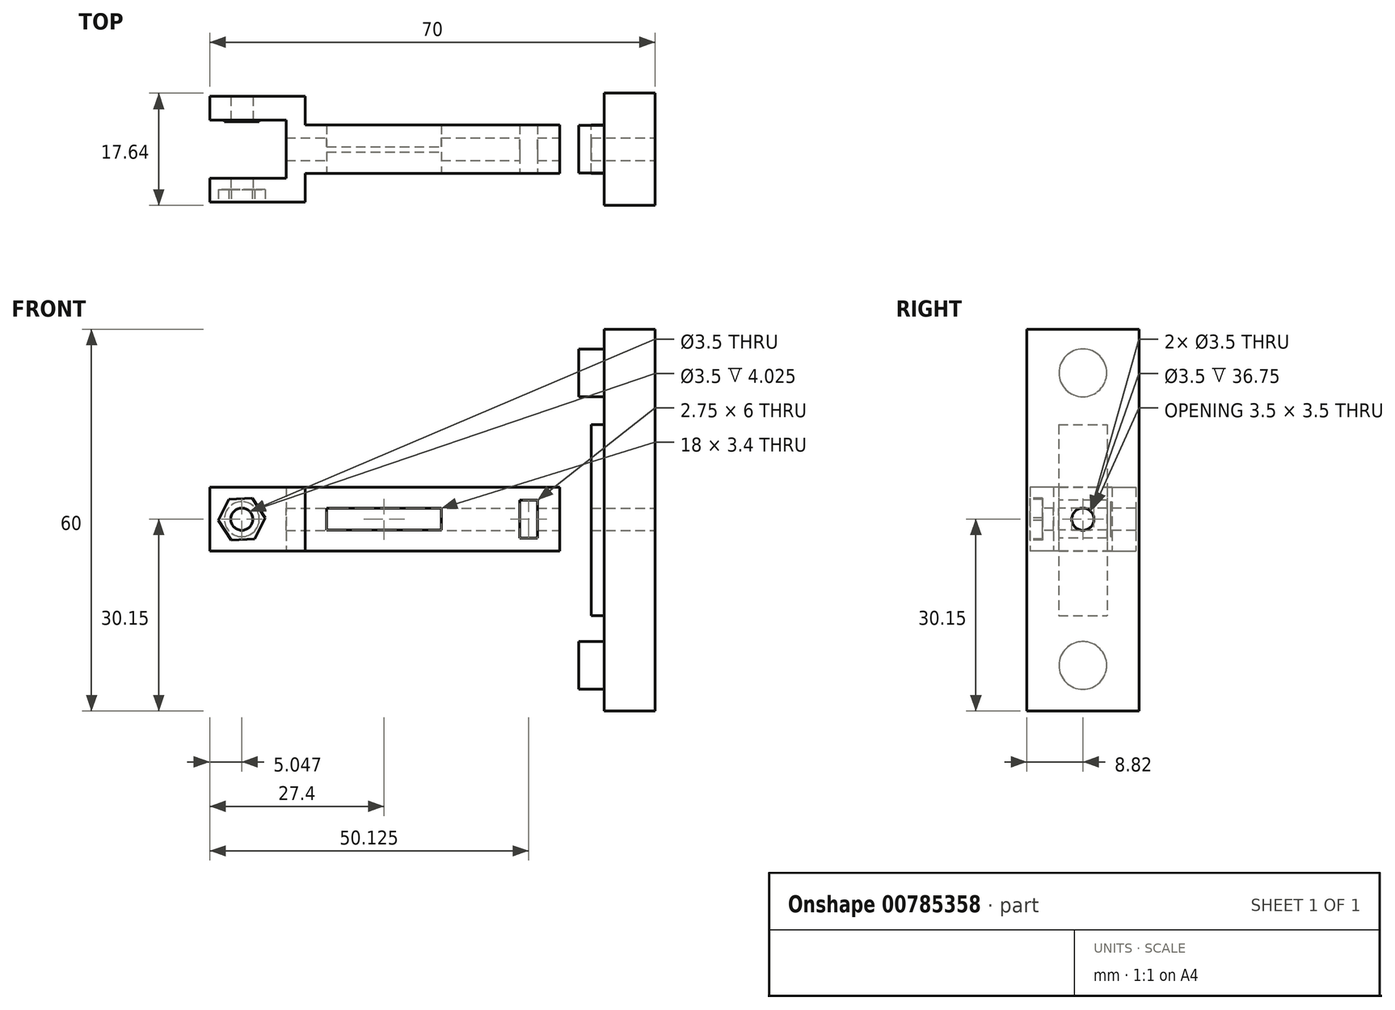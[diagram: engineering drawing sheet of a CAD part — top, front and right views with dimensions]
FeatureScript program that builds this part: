
annotation { "Feature Type Name" : "Feature", "Feature Type Description" : "" }
export const myFeature = defineFeature(function(context is Context, id is Id, definition is map)
    precondition{}
    {
        {
            var Q0;
            Q0=qCreatedBy(makeId("Top.planeOp"),FACE);
            var sketch = newSketch(context, id + "F0", { "sketchPlane" : qUnion([Q0])});
            skLineSegment(sketch, "E0.bottom", {"start": v(0, 0) * mm, "end": v(40, 0) * mm});
            skLineSegment(sketch, "E0.top", {"start": v(0, -3.83) * mm, "end": v(40, -3.83) * mm});
            skLineSegment(sketch, "E0.left", {"start": v(0, 0) * mm, "end": v(0, -3.83) * mm});
            skLineSegment(sketch, "E0.right", {"start": v(40, 0) * mm, "end": v(40, -3.83) * mm});
            skLineSegment(sketch, "E1.bottom", {"start": v(-3, 0) * mm, "end": v(0, 0) * mm});
            skLineSegment(sketch, "E1.top", {"start": v(-15, -8.32) * mm, "end": v(0, -8.32) * mm});
            skLineSegment(sketch, "E1.left", {"start": v(-15, -4.6) * mm, "end": v(-15, -8.32) * mm});
            skLineSegment(sketch, "E1.right", {"start": v(0, 0) * mm, "end": v(0, -8.32) * mm});
            skLineSegment(sketch, "E2.top", {"start": v(-15, -4.6) * mm, "end": v(-3, -4.6) * mm});
            skLineSegment(sketch, "E2.right", {"start": v(-3, 0) * mm, "end": v(-3, -4.6) * mm});
            skLineSegment(sketch, "E3.MirrorCS", {"start": v(0, 0) * mm, "end": v(0, 3.83) * mm});
            skLineSegment(sketch, "E4.MirrorCS", {"start": v(0, 0) * mm, "end": v(0, 8.32) * mm});
            skLineSegment(sketch, "E5.MirrorCS", {"start": v(-15, 4.6) * mm, "end": v(-15, 8.32) * mm});
            skLineSegment(sketch, "E6.MirrorCS", {"start": v(-3, 0) * mm, "end": v(-3, 4.6) * mm});
            skLineSegment(sketch, "E7.MirrorCS", {"start": v(-15, 8.32) * mm, "end": v(0, 8.32) * mm});
            skLineSegment(sketch, "E8.MirrorCS", {"start": v(-15, 4.6) * mm, "end": v(-3, 4.6) * mm});
            skLineSegment(sketch, "E9.MirrorCS", {"start": v(40, 0) * mm, "end": v(40, 3.83) * mm});
            skLineSegment(sketch, "E10.MirrorCS", {"start": v(0, 3.83) * mm, "end": v(40, 3.83) * mm});
            skSolve(sketch);
        }
        {
            var Q0;
            Q0=makeQuery(id+"F0.imprint","IMPRINT",FACE,{"disambiguationData":[TD([[makeQuery(id+"F0.imprint","IMPRINT",EDGE,{"derivedFrom":sQuery(id+"F0.wireOp",EDGE,"E0.left")}),-1.0]])]});
            var Q1;
            Q1=makeQuery(id+"F0.imprint","IMPRINT",FACE,{"disambiguationData":[TD([[makeQuery(id+"F0.imprint","IMPRINT",EDGE,{"derivedFrom":sQuery(id+"F0.wireOp",EDGE,"E1.bottom")}),1.0]])]});
            var Q2;
            Q2=makeQuery(id+"F0.imprint","IMPRINT",FACE,{"disambiguationData":[TD([[makeQuery(id+"F0.imprint","IMPRINT",EDGE,{"derivedFrom":sQuery(id+"F0.wireOp",EDGE,"E0.bottom")}),1.0]])]});
            var Q3;
            Q3=makeQuery(id+"F0.imprint","IMPRINT",FACE,{"disambiguationData":[TD([[makeQuery(id+"F0.imprint","IMPRINT",EDGE,{"derivedFrom":sQuery(id+"F0.wireOp",EDGE,"E0.bottom")}),-1.0]])]});
            extrude(context, id + "F1", {"entities" : qUnion([Q0, Q1, Q2, Q3]), "depth" : 10 * mm});
        }
        {
            var Q0;
            Q0=makeQuery(id+"F1.opExtrude","SWEPT_FACE",FACE,{"disambiguationData":[OSD([sQuery(id+"F0.wireOp",EDGE,"E1.top")])]});
            var sketch = newSketch(context, id + "F2", { "sketchPlane" : qUnion([Q0])});
            skCircle(sketch, "E11", {"center": v(-9.95, 5) * mm, "radius": 1.75 * mm});
            skSolve(sketch);
        }
        {
            var Q0;
            Q0=makeQuery(id+"F2.imprint","IMPRINT",FACE,{"disambiguationData":[TD([[makeQuery(id+"F2.imprint","IMPRINT",EDGE,{"derivedFrom":sQuery(id+"F2.wireOp",EDGE,"E11")}),1.0]])]});
            extrude(context, id + "F3", {"entities" : qUnion([Q0]), "operationType" : NewBodyOperationType.REMOVE, "endBound" : BoundingType.THROUGH_ALL, "oppositeDirection" : true, "depth" : 25 * mm});
        }
        {
            var Q0;
            Q0=makeQuery(id+"F1.opExtrude","SWEPT_FACE",FACE,{"disambiguationData":[OSD([sQuery(id+"F0.wireOp",EDGE,"E0.top")])]});
            var sketch = newSketch(context, id + "F4", { "sketchPlane" : qUnion([Q0])});
            skLineSegment(sketch, "E12.bottom", {"start": v(3.4, 3.3) * mm, "end": v(21.4, 3.3) * mm});
            skLineSegment(sketch, "E12.top", {"start": v(3.4, 6.7) * mm, "end": v(21.4, 6.7) * mm});
            skLineSegment(sketch, "E12.left", {"start": v(3.4, 3.3) * mm, "end": v(3.4, 6.7) * mm});
            skLineSegment(sketch, "E12.right", {"start": v(21.4, 3.3) * mm, "end": v(21.4, 6.7) * mm});
            skLineSegment(sketch, "E13.bottom", {"start": v(33.75, 8) * mm, "end": v(36.5, 8) * mm});
            skLineSegment(sketch, "E13.top", {"start": v(33.75, 2) * mm, "end": v(36.5, 2) * mm});
            skLineSegment(sketch, "E13.left", {"start": v(33.75, 8) * mm, "end": v(33.75, 2) * mm});
            skLineSegment(sketch, "E13.right", {"start": v(36.5, 8) * mm, "end": v(36.5, 2) * mm});
            skSolve(sketch);
        }
        {
            var Q0;
            Q0=makeQuery(id+"F4.imprint","IMPRINT",FACE,{"disambiguationData":[TD([[makeQuery(id+"F4.imprint","IMPRINT",EDGE,{"derivedFrom":sQuery(id+"F4.wireOp",EDGE,"E12.bottom")}),1.0]])]});
            var Q1;
            Q1=makeQuery(id+"F4.imprint","IMPRINT",FACE,{"disambiguationData":[TD([[makeQuery(id+"F4.imprint","IMPRINT",EDGE,{"derivedFrom":sQuery(id+"F4.wireOp",EDGE,"E13.bottom")}),-1.0]])]});
            extrude(context, id + "F5", {"entities" : qUnion([Q0, Q1]), "operationType" : NewBodyOperationType.REMOVE, "endBound" : BoundingType.THROUGH_ALL, "oppositeDirection" : true, "depth" : 25 * mm});
        }
        {
            var Q0;
            Q0=makeQuery(id+"F1.opExtrude","SWEPT_FACE",FACE,{"disambiguationData":[OSD([sQuery(id+"F0.wireOp",EDGE,"E0.right"),sQuery(id+"F0.wireOp",EDGE,"E9.MirrorCS")])]});
            var sketch = newSketch(context, id + "F6", { "sketchPlane" : qUnion([Q0])});
            skCircle(sketch, "E14", {"center": v(0, 5) * mm, "radius": 1.75 * mm});
            skSolve(sketch);
        }
        {
            var Q0;
            Q0=makeQuery(id+"F6.imprint","IMPRINT",FACE,{"disambiguationData":[TD([[makeQuery(id+"F6.imprint","IMPRINT",EDGE,{"derivedFrom":sQuery(id+"F6.wireOp",EDGE,"E14")}),1.0]])]});
            extrude(context, id + "F7", {"entities" : qUnion([Q0]), "operationType" : NewBodyOperationType.REMOVE, "oppositeDirection" : true, "depth" : 15 * mm});
        }
        {
            var Q0;
            Q0=makeQuery(id+"F1.opExtrude","SWEPT_FACE",FACE,{"disambiguationData":[OSD([sQuery(id+"F0.wireOp",EDGE,"E0.right"),sQuery(id+"F0.wireOp",EDGE,"E9.MirrorCS")])]});
            cPlane(context, id + "F8", {"entities" : qUnion([Q0]), "cplaneType" : CPlaneType.OFFSET, "offset" : 5 * mm, "width" : 150 * mm, "height" : 150 * mm});
        }
        {
            var Q0;
            Q0=qCreatedBy(id+"F8.planeOp",FACE);
            var sketch = newSketch(context, id + "F9", { "sketchPlane" : qUnion([Q0])});
            skLineSegment(sketch, "E15.0", {"start": v(3.83, 10) * mm, "end": v(3.83, 0) * mm});
            skLineSegment(sketch, "E16.0", {"start": v(-3.83, 10) * mm, "end": v(-3.83, 0) * mm});
            skLineSegment(sketch, "E17.bottom", {"start": v(-3.82, 19.85) * mm, "end": v(3.82, 19.85) * mm});
            skLineSegment(sketch, "E17.top", {"start": v(-3.82, -10.15) * mm, "end": v(3.82, -10.15) * mm});
            skLineSegment(sketch, "E17.left", {"start": v(-3.83, 19.85) * mm, "end": v(-3.82, -10.15) * mm});
            skLineSegment(sketch, "E17.right", {"start": v(3.82, 19.85) * mm, "end": v(3.83, -10.15) * mm});
            skPoint(sketch, "E18.oppositeSnap0", {"position": v(3.83, 4.85) * mm});
            skLineSegment(sketch, "E18.bottom", {"start": v(3.83, 4.85) * mm, "end": v(3.83, 4.85) * mm});
            skLineSegment(sketch, "E18.top", {"start": v(3.83, 4.85) * mm, "end": v(3.83, 4.85) * mm});
            skLineSegment(sketch, "E18.left", {"start": v(3.83, 4.85) * mm, "end": v(3.83, 4.85) * mm});
            skLineSegment(sketch, "E18.right", {"start": v(3.83, 4.85) * mm, "end": v(3.83, 4.85) * mm});
            skSolve(sketch);
        }
        {
            var Q0;
            {var subQ0=sQuery(id+"F9.wireOp",EDGE,"E17.bottom");Q0=makeQuery(id+"F9.imprint","IMPRINT",FACE,{"disambiguationData":[TD([[makeQuery(id+"F9.imprint","IMPRINT",EDGE,{"derivedFrom":subQ0}),-1.0]])]});}
            extrude(context, id + "F10", {"entities" : qUnion([Q0]), "depth" : 2 * mm});
        }
        {
            var Q0;
            Q0=makeQuery(id+"F10.opExtrude","CAP_FACE",FACE,{"disambiguationData":[OSD([sQuery(id+"F9.wireOp",EDGE,"E17.bottom"),sQuery(id+"F9.wireOp",EDGE,"E17.top"),sQuery(id+"F9.wireOp",EDGE,"E17.left"),sQuery(id+"F9.wireOp",EDGE,"E17.right")])],"isStart":false});
            var sketch = newSketch(context, id + "F11", { "sketchPlane" : qUnion([Q0])});
            skLineSegment(sketch, "E19.bottom", {"start": v(8.82, 34.85) * mm, "end": v(-8.83, 34.85) * mm});
            skLineSegment(sketch, "E19.top", {"start": v(8.83, -25.15) * mm, "end": v(-8.82, -25.15) * mm});
            skLineSegment(sketch, "E19.left", {"start": v(8.82, 34.85) * mm, "end": v(8.83, -25.15) * mm});
            skLineSegment(sketch, "E19.right", {"start": v(-8.83, 34.85) * mm, "end": v(-8.82, -25.15) * mm});
            skSolve(sketch);
        }
        {
            var Q0;
            Q0=qSketchRegion(id+"F11",true);
            extrude(context, id + "F12", {"entities" : qUnion([Q0]), "operationType" : NewBodyOperationType.ADD, "depth" : 8 * mm});
        }
        {
            var Q0;
            Q0=makeQuery(id+"F12.opExtrude","CAP_FACE",FACE,{"disambiguationData":[OSD([sQuery(id+"F11.wireOp",EDGE,"E19.bottom"),sQuery(id+"F11.wireOp",EDGE,"E19.top"),sQuery(id+"F11.wireOp",EDGE,"E19.left"),sQuery(id+"F11.wireOp",EDGE,"E19.right")])],"isStart":false});
            var sketch = newSketch(context, id + "F13", { "sketchPlane" : qUnion([Q0])});
            skCircle(sketch, "E20.0", {"center": v(0, 5) * mm, "radius": 1.75 * mm});
            skSolve(sketch);
        }
        {
            var Q0;
            Q0=makeQuery(id+"F13.imprint","IMPRINT",FACE,{"disambiguationData":[TD([[makeQuery(id+"F13.imprint","IMPRINT",EDGE,{"derivedFrom":sQuery(id+"F13.wireOp",EDGE,"E20.0")}),1.0]])]});
            extrude(context, id + "F14", {"entities" : qUnion([Q0]), "operationType" : NewBodyOperationType.REMOVE, "endBound" : BoundingType.THROUGH_ALL, "oppositeDirection" : true, "depth" : 25 * mm});
        }
        {
            var Q0;
            Q0=makeQuery(id+"F1.opExtrude","SWEPT_FACE",FACE,{"disambiguationData":[OSD([sQuery(id+"F0.wireOp",EDGE,"E8.MirrorCS")])]});
            var sketch = newSketch(context, id + "F15", { "sketchPlane" : qUnion([Q0])});
            skCircle(sketch, "E21", {"center": v(-9.95, 5) * mm, "radius": 1.75 * mm});
            skCircle(sketch, "E22", {"center": v(-9.95, 5) * mm, "radius": 2.75 * mm});
            skSolve(sketch);
        }
        {
            var Q0;
            Q0=makeQuery(id+"F15.imprint","IMPRINT",FACE,{"disambiguationData":[TD([[makeQuery(id+"F15.imprint","IMPRINT",EDGE,{"derivedFrom":sQuery(id+"F15.wireOp",EDGE,"E21")}),1.0]])]});
            extrude(context, id + "F16", {"entities" : qUnion([Q0]), "operationType" : NewBodyOperationType.ADD, "depth" : 0.3 * mm});
        }
        {
            var Q0;
            Q0=makeQuery(id+"F1.opExtrude","SWEPT_FACE",FACE,{"disambiguationData":[OSD([sQuery(id+"F0.wireOp",EDGE,"E1.top")])]});
            var sketch = newSketch(context, id + "F17", { "sketchPlane" : qUnion([Q0])});
            skCircle(sketch, "E23.cCircle", {"center": v(-9.95, 5) * mm, "radius": 3.2 * mm, "construction": true});
            skLineSegment(sketch, "E23.0", {"start": v(-6.26, 5.2) * mm, "end": v(-7.93, 1.9) * mm});
            skLineSegment(sketch, "E23.1", {"start": v(-7.93, 1.9) * mm, "end": v(-11.62, 1.7) * mm});
            skLineSegment(sketch, "E23.2", {"start": v(-11.62, 1.7) * mm, "end": v(-13.64, 4.8) * mm});
            skLineSegment(sketch, "E23.3", {"start": v(-13.64, 4.8) * mm, "end": v(-11.98, 8.1) * mm});
            skLineSegment(sketch, "E23.4", {"start": v(-11.98, 8.1) * mm, "end": v(-8.29, 8.3) * mm});
            skLineSegment(sketch, "E23.5", {"start": v(-8.29, 8.3) * mm, "end": v(-6.26, 5.2) * mm});
            skPoint(sketch, "E23.0.midPoint", {"position": v(-7.1, 3.56) * mm});
            skSolve(sketch);
        }
        {
            var Q0;
            Q0=makeQuery(id+"F17.imprint","IMPRINT",FACE,{"disambiguationData":[TD([[makeQuery(id+"F17.imprint","IMPRINT",EDGE,{"derivedFrom":sQuery(id+"F17.wireOp",EDGE,"E23.0")}),-1.0]])]});
            extrude(context, id + "F18", {"entities" : qUnion([Q0]), "operationType" : NewBodyOperationType.REMOVE, "oppositeDirection" : true, "depth" : 2 * mm});
        }
        {
            var Q0;
            Q0=makeQuery(id+"F12.opExtrude","CAP_FACE",FACE,{"disambiguationData":[OSD([sQuery(id+"F11.wireOp",EDGE,"E19.bottom"),sQuery(id+"F11.wireOp",EDGE,"E19.top"),sQuery(id+"F11.wireOp",EDGE,"E19.left"),sQuery(id+"F11.wireOp",EDGE,"E19.right")])],"isStart":true});
            var sketch = newSketch(context, id + "F19", { "sketchPlane" : qUnion([Q0])});
            skCircle(sketch, "E24.0", {"center": v(0, 5) * mm, "radius": 1.75 * mm});
            skCircle(sketch, "E25", {"center": v(0, -18) * mm, "radius": 3.75 * mm});
            skCircle(sketch, "E26", {"center": v(0, 28) * mm, "radius": 3.75 * mm});
            skSolve(sketch);
        }
        {
            var Q0;
            Q0=makeQuery(id+"F19.imprint","IMPRINT",FACE,{"disambiguationData":[TD([[makeQuery(id+"F19.imprint","IMPRINT",EDGE,{"derivedFrom":sQuery(id+"F19.wireOp",EDGE,"E26")}),1.0]])]});
            var Q1;
            Q1=makeQuery(id+"F19.imprint","IMPRINT",FACE,{"disambiguationData":[TD([[makeQuery(id+"F19.imprint","IMPRINT",EDGE,{"derivedFrom":sQuery(id+"F19.wireOp",EDGE,"E25")}),1.0]])]});
            extrude(context, id + "F20", {"entities" : qUnion([Q0, Q1]), "operationType" : NewBodyOperationType.ADD, "depth" : 4 * mm});
        }
    });
